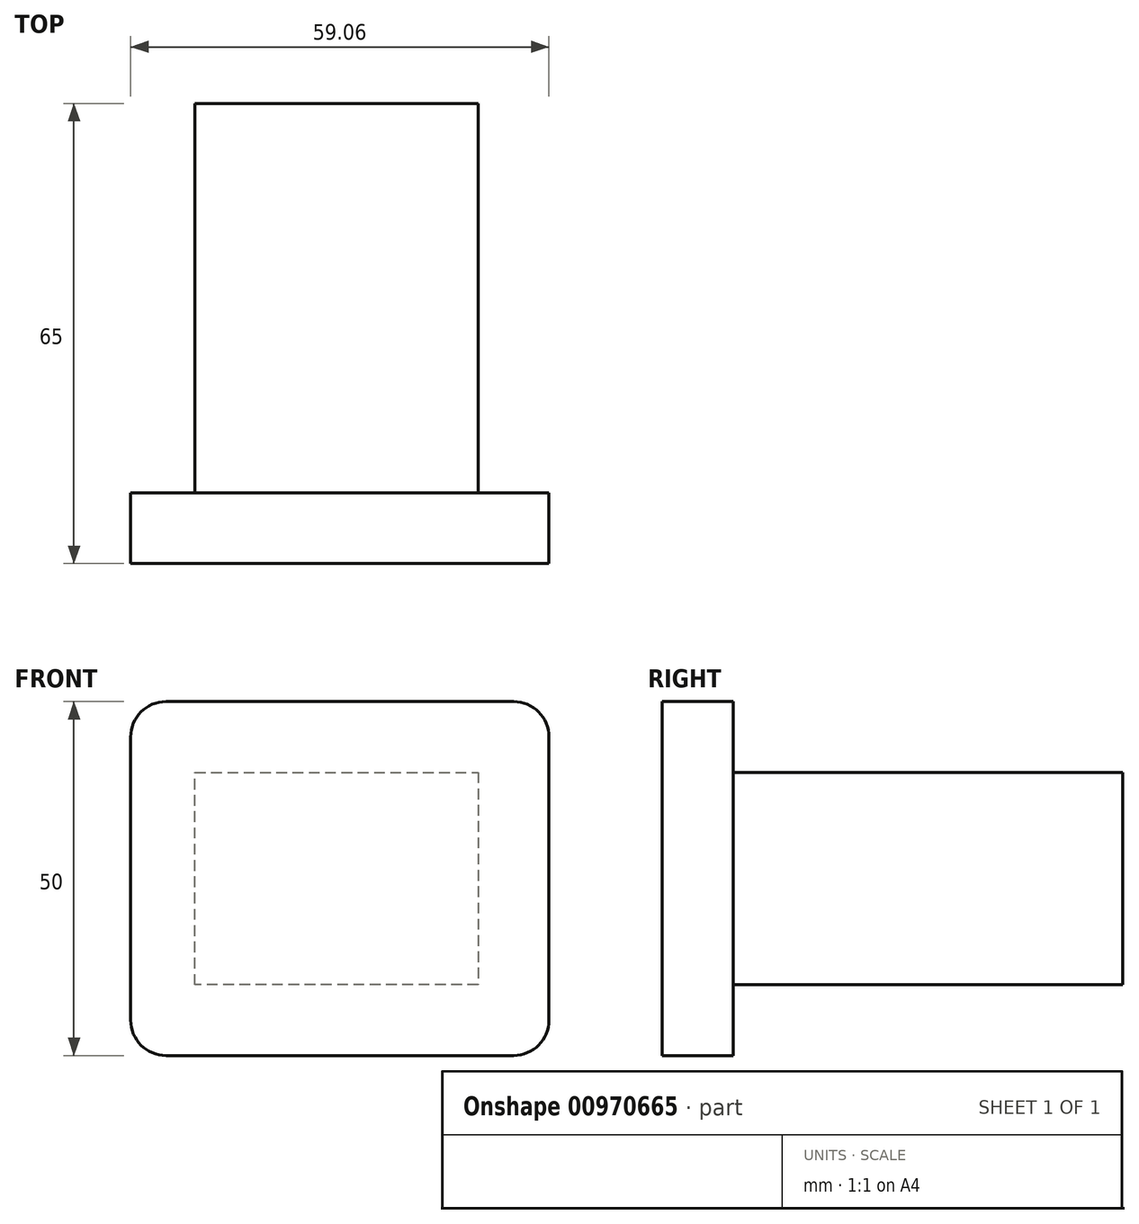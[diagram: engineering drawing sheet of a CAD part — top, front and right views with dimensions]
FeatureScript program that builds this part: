
annotation { "Feature Type Name" : "Feature", "Feature Type Description" : "" }
export const myFeature = defineFeature(function(context is Context, id is Id, definition is map)
    precondition{}
    {
        {
            var Q0;
            Q0=qCreatedBy(makeId("Front.planeOp"),FACE);
            var sketch = newSketch(context, id + "F0", { "sketchPlane" : qUnion([Q0])});
            skLineSegment(sketch, "E0", {"start": v(-23.41, 14.97) * mm, "end": v(25.65, 14.97) * mm});
            skLineSegment(sketch, "E1", {"start": v(30.65, 9.97) * mm, "end": v(30.65, -30.03) * mm});
            skLineSegment(sketch, "E2", {"start": v(25.65, -35.03) * mm, "end": v(-23.41, -35.03) * mm});
            skLineSegment(sketch, "E3", {"start": v(-28.41, -30.03) * mm, "end": v(-28.41, 9.97) * mm});
            skPoint(sketch, "E4.newPointA", {"position": v(-29.35, 14.97) * mm});
            skArc(sketch, "E4.filletArc", {"start": v(-23.41, 14.97) * mm, "mid": v(-26.95, 13.5) * mm, "end": v(-28.41, 9.97) * mm});
            skPoint(sketch, "E5.visualSharp", {"position": v(30.65, 14.97) * mm});
            skArc(sketch, "E5.filletArc", {"start": v(30.65, 9.97) * mm, "mid": v(29.19, 13.5) * mm, "end": v(25.65, 14.97) * mm});
            skPoint(sketch, "E6.visualSharp", {"position": v(-28.41, -35.03) * mm});
            skArc(sketch, "E6.filletArc", {"start": v(-28.41, -30.03) * mm, "mid": v(-26.95, -33.57) * mm, "end": v(-23.41, -35.03) * mm});
            skPoint(sketch, "E7.visualSharp", {"position": v(30.65, -35.03) * mm});
            skArc(sketch, "E7.filletArc", {"start": v(25.65, -35.03) * mm, "mid": v(29.19, -33.57) * mm, "end": v(30.65, -30.03) * mm});
            skSolve(sketch);
        }
        {
            var Q0;
            Q0=makeQuery(id+"F0.imprint","IMPRINT",FACE,{"disambiguationData":[TD([[makeQuery(id+"F0.imprint","IMPRINT",EDGE,{"derivedFrom":sQuery(id+"F0.wireOp",EDGE,"E0")}),-1.0]])]});
            extrude(context, id + "F1", {"entities" : qUnion([Q0]), "depth" : 10 * mm, "offsetDistance" : 25 * mm});
        }
        {
            var Q0;
            Q0=qCreatedBy(makeId("Front.planeOp"),FACE);
            var sketch = newSketch(context, id + "F2", { "sketchPlane" : qUnion([Q0])});
            skLineSegment(sketch, "E8", {"start": v(-19.35, 4.97) * mm, "end": v(20.65, 4.97) * mm});
            skLineSegment(sketch, "E9", {"start": v(20.65, 4.97) * mm, "end": v(20.65, -25.03) * mm});
            skLineSegment(sketch, "E10", {"start": v(20.65, -25.03) * mm, "end": v(-19.35, -25.03) * mm});
            skLineSegment(sketch, "E11", {"start": v(-19.35, -25.03) * mm, "end": v(-19.35, 4.97) * mm});
            skSolve(sketch);
        }
        {
            var Q0;
            Q0 = qSketchRegion(id + "F2", true);
            extrude(context, id + "F3", {"entities" : qUnion([Q0]), "operationType" : NewBodyOperationType.ADD, "oppositeDirection" : true, "depth" : 55 * mm, "offsetDistance" : 25 * mm});
        }
    });
